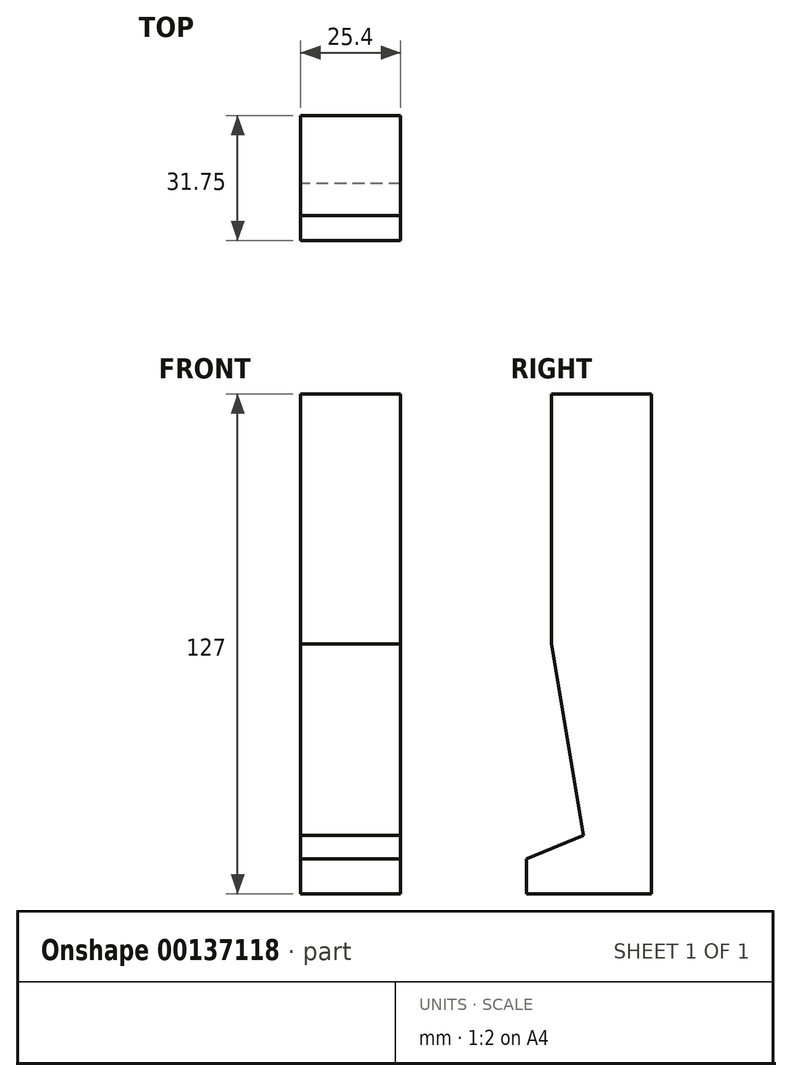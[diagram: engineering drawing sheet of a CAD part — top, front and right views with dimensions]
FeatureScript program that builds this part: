
annotation { "Feature Type Name" : "Feature", "Feature Type Description" : "" }
export const myFeature = defineFeature(function(context is Context, id is Id, definition is map)
    precondition{}
    {
        {
            var Q0;
            Q0=qCreatedBy(makeId("Right.planeOp"),FACE);
            var sketch = newSketch(context, id + "F0", { "sketchPlane" : qUnion([Q0])});
            skLineSegment(sketch, "E0", {"start": v(-12.7, 0) * mm, "end": v(-12.7, 63.5) * mm});
            skLineSegment(sketch, "E1", {"start": v(-12.7, 63.5) * mm, "end": v(12.7, 63.5) * mm});
            skLineSegment(sketch, "E2", {"start": v(12.7, 63.5) * mm, "end": v(12.7, 0) * mm});
            skLineSegment(sketch, "E3", {"start": v(12.7, 0) * mm, "end": v(12.7, -63.5) * mm});
            skLineSegment(sketch, "E4", {"start": v(12.7, -63.5) * mm, "end": v(-19.05, -63.5) * mm});
            skLineSegment(sketch, "E5", {"start": v(-19.05, -63.5) * mm, "end": v(-19.05, -54.6) * mm});
            skLineSegment(sketch, "E6", {"start": v(-19.05, -54.6) * mm, "end": v(-4.57, -48.67) * mm});
            skLineSegment(sketch, "E7", {"start": v(-4.57, -48.67) * mm, "end": v(-12.7, 0) * mm});
            skLineSegment(sketch, "E8", {"start": v(-12.7, 0) * mm, "end": v(12.7, 0) * mm, "construction": true});
            skSolve(sketch);
        }
        {
            var Q0;
            Q0 = qSketchRegion(id + "F0", true);
            extrude(context, id + "F1", {"entities" : qUnion([Q0]), "depth" : 25.4 * mm});
        }
    });
